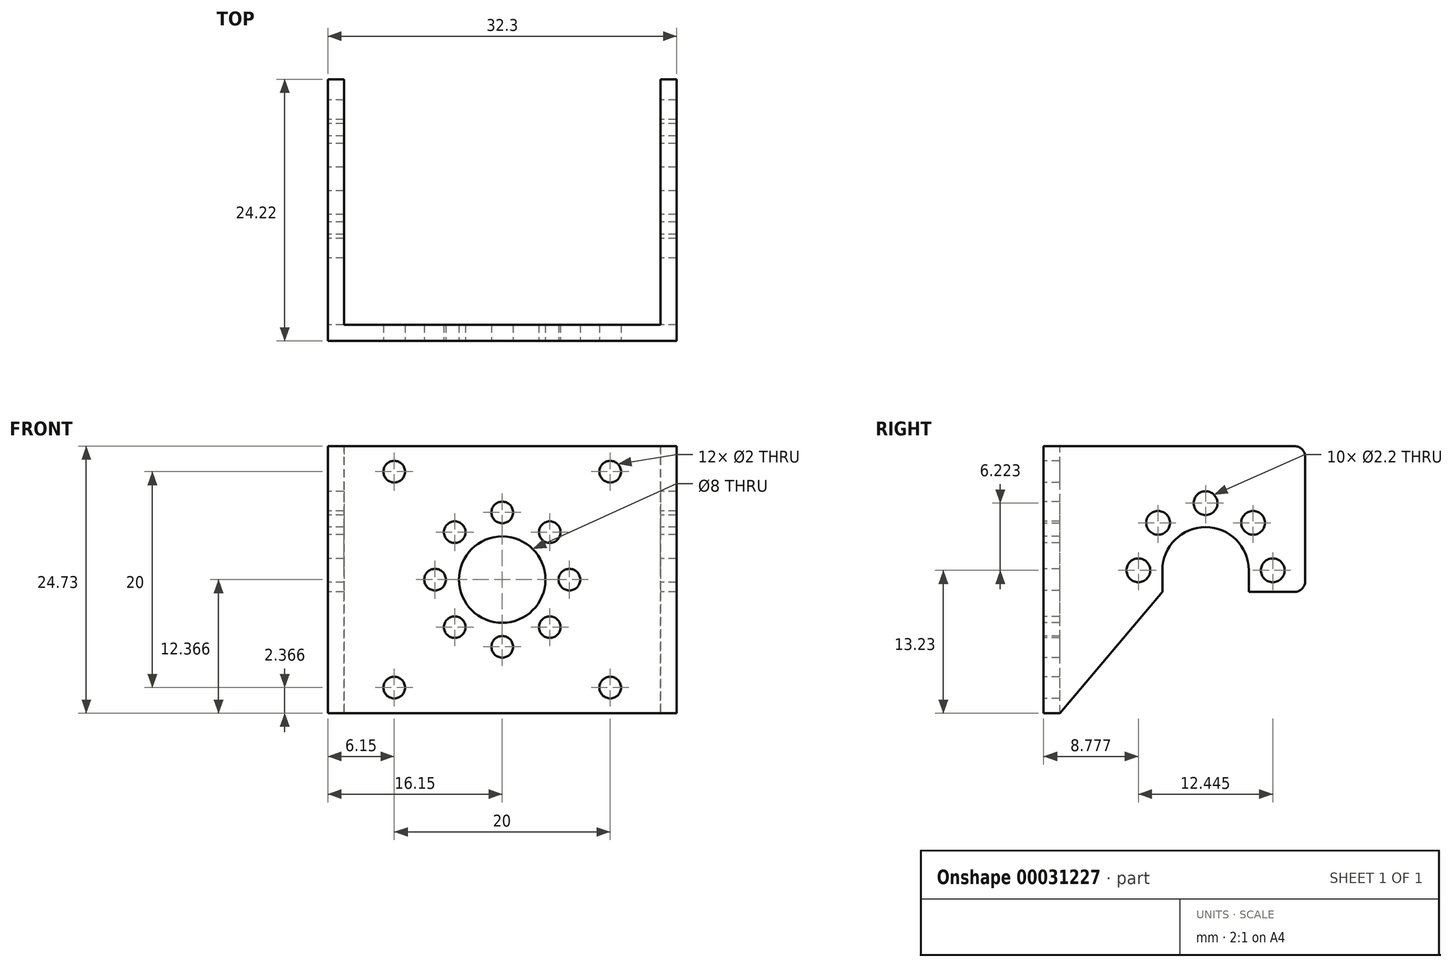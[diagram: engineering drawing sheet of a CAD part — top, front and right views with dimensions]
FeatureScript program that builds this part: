
annotation { "Feature Type Name" : "Feature", "Feature Type Description" : "" }
export const myFeature = defineFeature(function(context is Context, id is Id, definition is map)
    precondition{}
    {
        {
            var Q0;
            Q0=qCreatedBy(makeId("Front.planeOp"),FACE);
            var sketch = newSketch(context, id + "F0", { "sketchPlane" : qUnion([Q0])});
            skLineSegment(sketch, "E0.bottom", {"start": v(0, 0) * mm, "end": v(1.5, 0) * mm});
            skLineSegment(sketch, "E0.top", {"start": v(0, 41.5) * mm, "end": v(32.3, 41.5) * mm});
            skLineSegment(sketch, "E0.left", {"start": v(0, 0) * mm, "end": v(0, 41.5) * mm});
            skLineSegment(sketch, "E0.right", {"start": v(32.3, 0) * mm, "end": v(32.3, 41.5) * mm});
            skLineSegment(sketch, "E1.top", {"start": v(1.5, 40) * mm, "end": v(30.8, 40) * mm});
            skLineSegment(sketch, "E1.left", {"start": v(1.5, 0) * mm, "end": v(1.5, 40) * mm});
            skLineSegment(sketch, "E1.right", {"start": v(30.8, 0) * mm, "end": v(30.8, 40) * mm});
            skLineSegment(sketch, "E2.trimOffspring", {"start": v(30.8, 0) * mm, "end": v(32.3, 0) * mm});
            skSolve(sketch);
        }
        {
            var Q0;
            Q0=qSketchRegion(id+"F0",true);
            extrude(context, id + "F1", {"entities" : qUnion([Q0]), "depth" : 30 * mm});
        }
        {
            var Q0;
            Q0=makeQuery(id+"F1.opExtrude","SWEPT_FACE",FACE,{"disambiguationData":[OSD([sQuery(id+"F0.wireOp",EDGE,"E0.left")])]});
            var sketch = newSketch(context, id + "F2", { "sketchPlane" : qUnion([Q0])});
            skArc(sketch, "E3", {"start": v(19, 15) * mm, "mid": v(15, 19) * mm, "end": v(11, 15) * mm});
            skCircle(sketch, "E4", {"center": v(21.22, 15) * mm, "radius": 1.1 * mm});
            skCircle(sketch, "E5.1.0", {"center": v(19.4, 19.4) * mm, "radius": 1.1 * mm});
            skCircle(sketch, "E5.2.0", {"center": v(15, 21.22) * mm, "radius": 1.1 * mm});
            skCircle(sketch, "E5.3.0", {"center": v(10.6, 19.4) * mm, "radius": 1.1 * mm});
            skCircle(sketch, "E5.4.0", {"center": v(8.78, 15) * mm, "radius": 1.1 * mm});
            skLineSegment(sketch, "E6", {"start": v(11, 15) * mm, "end": v(11, 0) * mm});
            skLineSegment(sketch, "E7", {"start": v(19, 15) * mm, "end": v(19, 0) * mm});
            skLineSegment(sketch, "E8", {"start": v(11, 0) * mm, "end": v(19, 0) * mm});
            skLineSegment(sketch, "E9", {"start": v(15, 41.5) * mm, "end": v(15, 0) * mm, "construction": true});
            skPoint(sketch, "E10", {"position": v(15, 0) * mm});
            skLineSegment(sketch, "E11", {"start": v(6.78, 0) * mm, "end": v(0, 0) * mm});
            skLineSegment(sketch, "E12", {"start": v(0, 0) * mm, "end": v(0, 40) * mm});
            skLineSegment(sketch, "E13.MirrorCS", {"start": v(30, 0) * mm, "end": v(30, 40) * mm});
            skLineSegment(sketch, "E14.MirrorCS", {"start": v(23.22, 0) * mm, "end": v(30, 0) * mm});
            skPoint(sketch, "E15.MirrorCS.end.orphan", {"position": v(30, 40) * mm});
            skPoint(sketch, "E15.MirrorCS.start.orphan", {"position": v(23.22, 0) * mm});
            skSolve(sketch);
        }
        {
            var Q0;
            Q0=qSketchRegion(id+"F2",true);
            extrude(context, id + "F3", {"entities" : qUnion([Q0]), "operationType" : NewBodyOperationType.REMOVE, "endBound" : BoundingType.THROUGH_ALL, "oppositeDirection" : true, "depth" : 25 * mm});
        }
        {
            var Q0;
            Q0=makeQuery(id+"F1.opExtrude","SWEPT_FACE",FACE,{"disambiguationData":[OSD([sQuery(id+"F0.wireOp",EDGE,"E1.top")])]});
            var sketch = newSketch(context, id + "F4", { "sketchPlane" : qUnion([Q0])});
            skLineSegment(sketch, "E16.bottom", {"start": v(1.5, 30) * mm, "end": v(30.8, 30) * mm});
            skLineSegment(sketch, "E16.top", {"start": v(1.5, 28.5) * mm, "end": v(30.8, 28.5) * mm});
            skLineSegment(sketch, "E16.left", {"start": v(1.5, 30) * mm, "end": v(1.5, 28.5) * mm});
            skLineSegment(sketch, "E16.right", {"start": v(30.8, 30) * mm, "end": v(30.8, 28.5) * mm});
            skSolve(sketch);
        }
        {
            var Q0;
            Q0 = qSketchRegion(id + "F4", true);
            extrude(context, id + "F5", {"entities" : qUnion([Q0]), "operationType" : NewBodyOperationType.ADD, "depth" : 40 * mm});
        }
        {
            var Q0;
            Q0=makeQuery(id+"F1.opExtrude","SWEPT_FACE",FACE,{"disambiguationData":[OSD([sQuery(id+"F0.wireOp",EDGE,"E0.left")])]});
            var sketch = newSketch(context, id + "F6", { "sketchPlane" : qUnion([Q0])});
            skLineSegment(sketch, "E17.bottom", {"start": v(0, 41.5) * mm, "end": v(30, 41.5) * mm});
            skLineSegment(sketch, "E17.top", {"start": v(5.78, 26.5) * mm, "end": v(30, 26.5) * mm});
            skLineSegment(sketch, "E17.left", {"start": v(0, 41.5) * mm, "end": v(0, 26.5) * mm});
            skLineSegment(sketch, "E17.right", {"start": v(30, 41.5) * mm, "end": v(30, 26.5) * mm});
            skLineSegment(sketch, "E18.top", {"start": v(0, 0) * mm, "end": v(5.78, 0) * mm});
            skLineSegment(sketch, "E18.left", {"start": v(0, 26.5) * mm, "end": v(0, 0) * mm});
            skLineSegment(sketch, "E18.right", {"start": v(5.78, 26.5) * mm, "end": v(5.78, 0) * mm});
            skPoint(sketch, "E19", {"position": v(8.78, 15) * mm});
            skLineSegment(sketch, "E20.bottom", {"start": v(5.78, 0) * mm, "end": v(11, 0) * mm});
            skLineSegment(sketch, "E20.top", {"start": v(5.78, 13) * mm, "end": v(11, 13) * mm});
            skLineSegment(sketch, "E20.left", {"start": v(5.78, 0) * mm, "end": v(5.78, 13) * mm});
            skLineSegment(sketch, "E20.right", {"start": v(11, 0) * mm, "end": v(11, 13) * mm});
            skLineSegment(sketch, "E21", {"start": v(19, 13) * mm, "end": v(30, 0) * mm});
            skLineSegment(sketch, "E22", {"start": v(30, 0) * mm, "end": v(19, 0) * mm});
            skLineSegment(sketch, "E23", {"start": v(19, 0) * mm, "end": v(19, 13) * mm});
            skLineSegment(sketch, "E24", {"start": v(30, 1.77) * mm, "end": v(28.5, 1.77) * mm});
            skSolve(sketch);
        }
        {
            var Q0;
            Q0 = qSketchRegion(id + "F6", true);
            var Q1;
            {var subQ3=sQuery(id+"F6.wireOp",EDGE,"E24");Q1=makeQuery(id+"F6.imprint","IMPRINT",FACE,{"disambiguationData":[TD([[makeQuery(id+"F6.imprint","IMPRINT",EDGE,{"derivedFrom":subQ3}),1.0]])]});}
            extrude(context, id + "F7", {"entities" : qUnion([Q0, Q1]), "operationType" : NewBodyOperationType.REMOVE, "endBound" : BoundingType.THROUGH_ALL, "oppositeDirection" : true, "depth" : 25 * mm});
        }
        {
            var Q0;
            Q0=makeQuery(id+"F5.boolean.opBoolean","MERGE",FACE,{"derivedFrom":[makeQuery(id+"F1.opExtrude","CAP_FACE",FACE,{"disambiguationData":[OSD([sQuery(id+"F0.wireOp",EDGE,"E0.bottom"),sQuery(id+"F0.wireOp",EDGE,"E0.top"),sQuery(id+"F0.wireOp",EDGE,"E0.left"),sQuery(id+"F0.wireOp",EDGE,"E0.right"),sQuery(id+"F0.wireOp",EDGE,"E1.top"),sQuery(id+"F0.wireOp",EDGE,"E1.left"),sQuery(id+"F0.wireOp",EDGE,"E1.right"),sQuery(id+"F0.wireOp",EDGE,"E2.trimOffspring")])],"isStart":false}),makeQuery(id+"F5.opExtrude","SWEPT_FACE",FACE,{"disambiguationData":[OSD([sQuery(id+"F4.wireOp",EDGE,"E16.bottom")])]})]});
            var sketch = newSketch(context, id + "F8", { "sketchPlane" : qUnion([Q0])});
            skLineSegment(sketch, "E25", {"start": v(0, 14.14) * mm, "end": v(32.3, 14.14) * mm, "construction": true});
            skCircle(sketch, "E26", {"center": v(6.15, 24.14) * mm, "radius": 1 * mm});
            skCircle(sketch, "E27.MirrorC", {"center": v(6.15, 4.14) * mm, "radius": 1 * mm});
            skLineSegment(sketch, "E28.0", {"start": v(32.3, 26.5) * mm, "end": v(0, 26.5) * mm, "construction": true});
            skLineSegment(sketch, "E29.0", {"start": v(32.3, 1.77) * mm, "end": v(0, 1.77) * mm, "construction": true});
            skLineSegment(sketch, "E30", {"start": v(16.15, 26.5) * mm, "end": v(16.15, 1.77) * mm, "construction": true});
            skCircle(sketch, "E31.MirrorC", {"center": v(26.15, 24.14) * mm, "radius": 1 * mm});
            skCircle(sketch, "E32.MirrorC", {"center": v(26.15, 4.14) * mm, "radius": 1 * mm});
            skCircle(sketch, "E33", {"center": v(16.15, 14.14) * mm, "radius": 4 * mm});
            skLineSegment(sketch, "E34.bottom", {"start": v(20.55, 9.74) * mm, "end": v(11.75, 9.74) * mm, "construction": true});
            skLineSegment(sketch, "E34.top", {"start": v(20.55, 18.54) * mm, "end": v(11.75, 18.54) * mm, "construction": true});
            skLineSegment(sketch, "E34.left", {"start": v(20.55, 9.74) * mm, "end": v(20.55, 18.54) * mm, "construction": true});
            skLineSegment(sketch, "E34.right", {"start": v(11.75, 9.74) * mm, "end": v(11.75, 18.54) * mm, "construction": true});
            skCircle(sketch, "E35", {"center": v(20.55, 18.54) * mm, "radius": 1 * mm});
            skCircle(sketch, "E36.1.0", {"center": v(16.15, 20.36) * mm, "radius": 1 * mm});
            skCircle(sketch, "E36.2.0", {"center": v(11.75, 18.54) * mm, "radius": 1 * mm});
            skCircle(sketch, "E36.3.0", {"center": v(9.93, 14.14) * mm, "radius": 1 * mm});
            skCircle(sketch, "E36.4.0", {"center": v(11.75, 9.74) * mm, "radius": 1 * mm});
            skCircle(sketch, "E36.5.0", {"center": v(16.15, 7.91) * mm, "radius": 1 * mm});
            skCircle(sketch, "E36.6.0", {"center": v(20.55, 9.74) * mm, "radius": 1 * mm});
            skCircle(sketch, "E36.7.0", {"center": v(22.37, 14.14) * mm, "radius": 1 * mm});
            skSolve(sketch);
        }
        {
            var Q0;
            Q0 = qSketchRegion(id + "F8", true);
            extrude(context, id + "F9", {"entities" : qUnion([Q0]), "operationType" : NewBodyOperationType.REMOVE, "endBound" : BoundingType.UP_TO_NEXT, "oppositeDirection" : true, "depth" : 25 * mm});
        }
        {
            var Q0;
            Q0=makeQuery(id+"F7.boolean.opBoolean","COPY",EDGE,{"disambiguationData":[OD(0.0)],"derivedFrom":makeQuery(id+"F7.opExtrude","SWEPT_EDGE",EDGE,{"disambiguationData":[OSD([sQuery(id+"F6.wireOp",EDGE,"E18.right"),sQuery(id+"F6.wireOp",EDGE,"E20.top"),sQuery(id+"F6.wireOp",EDGE,"E20.left")])]})});
            var Q1;
            Q1=makeQuery(id+"F7.boolean.opBoolean","COPY",EDGE,{"disambiguationData":[OD(0.0)],"derivedFrom":makeQuery(id+"F7.opExtrude","SWEPT_EDGE",EDGE,{"disambiguationData":[OSD([sQuery(id+"F2.wireOp",EDGE,"E7"),sQuery(id+"F6.wireOp",EDGE,"E21"),sQuery(id+"F6.wireOp",EDGE,"E23")])]})});
            var Q2;
            Q2=makeQuery(id+"F7.boolean.opBoolean","COPY",EDGE,{"disambiguationData":[OD(1.0)],"derivedFrom":makeQuery(id+"F7.opExtrude","SWEPT_EDGE",EDGE,{"disambiguationData":[OSD([sQuery(id+"F2.wireOp",EDGE,"E7"),sQuery(id+"F6.wireOp",EDGE,"E21"),sQuery(id+"F6.wireOp",EDGE,"E23")])]})});
            var Q3;
            Q3=makeQuery(id+"F7.boolean.opBoolean","COPY",EDGE,{"disambiguationData":[OD(1.0)],"derivedFrom":makeQuery(id+"F7.opExtrude","SWEPT_EDGE",EDGE,{"disambiguationData":[OSD([sQuery(id+"F6.wireOp",EDGE,"E18.right"),sQuery(id+"F6.wireOp",EDGE,"E20.top"),sQuery(id+"F6.wireOp",EDGE,"E20.left")])]})});
            var Q4;
            Q4=makeQuery(id+"F7.boolean.opBoolean","COPY",EDGE,{"disambiguationData":[OD(0.0)],"derivedFrom":makeQuery(id+"F7.opExtrude","SWEPT_EDGE",EDGE,{"disambiguationData":[OSD([sQuery(id+"F2.wireOp",EDGE,"E6"),sQuery(id+"F6.wireOp",EDGE,"E20.top"),sQuery(id+"F6.wireOp",EDGE,"E20.right")])]})});
            var Q5;
            Q5=makeQuery(id+"F7.boolean.opBoolean","COPY",EDGE,{"disambiguationData":[OD(1.0)],"derivedFrom":makeQuery(id+"F7.opExtrude","SWEPT_EDGE",EDGE,{"disambiguationData":[OSD([sQuery(id+"F2.wireOp",EDGE,"E6"),sQuery(id+"F6.wireOp",EDGE,"E20.top"),sQuery(id+"F6.wireOp",EDGE,"E20.right")])]})});
            var Q6;
            Q6=makeQuery(id+"F7.boolean.opBoolean","COPY",EDGE,{"disambiguationData":[OD(0.0)],"derivedFrom":makeQuery(id+"F7.opExtrude","SWEPT_EDGE",EDGE,{"disambiguationData":[OSD([sQuery(id+"F6.wireOp",EDGE,"E17.top"),sQuery(id+"F6.wireOp",EDGE,"E18.right")])]})});
            var Q7;
            Q7=makeQuery(id+"F7.boolean.opBoolean","COPY",EDGE,{"disambiguationData":[OD(1.0)],"derivedFrom":makeQuery(id+"F7.opExtrude","SWEPT_EDGE",EDGE,{"disambiguationData":[OSD([sQuery(id+"F6.wireOp",EDGE,"E17.top"),sQuery(id+"F6.wireOp",EDGE,"E18.right")])]})});
            fillet(context, id + "F10", {"entities" : qUnion([Q0, Q1, Q2, Q3, Q4, Q5, Q6, Q7]), "radius" : 1 * mm, "tangentPropagation" : true, "allowEdgeOverflow" : false});
        }
    });
